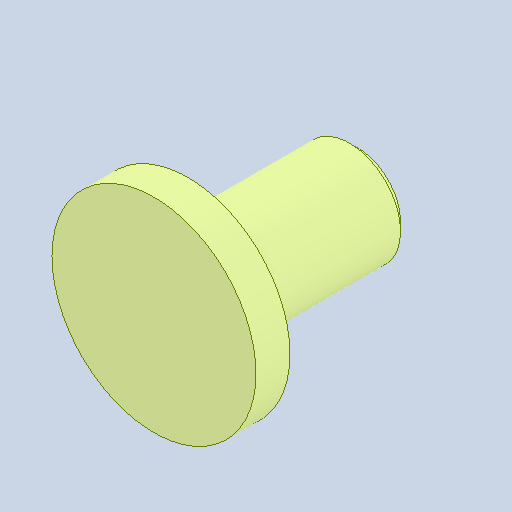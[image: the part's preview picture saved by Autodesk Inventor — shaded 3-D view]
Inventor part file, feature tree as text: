
AUTODESK INVENTOR PART (.ipt)
format: ipt  version: 2022 (Build 260153000, 153)  size: 93,184 bytes
history: native  units: in
note: dims shown in document units (in); Inventor stores cm internally (conversion verified against a paired STEP export)
features: other x3, sketch x2
ambient origin geometry x8: Origin, YZ Plane, XZ Plane, XY Plane, X Axis, Y Axis, Z Axis, Center Point
bodies: Solid1 (feature_tree)
feature tree (5):
  other  "pin.ipt"
  other  "Solid1::pin.ipt"
  other  "TaggingFeature1"
  sketch  "Sketch1"  dims[d0=0.3937in]
  sketch  "Sketch2"
